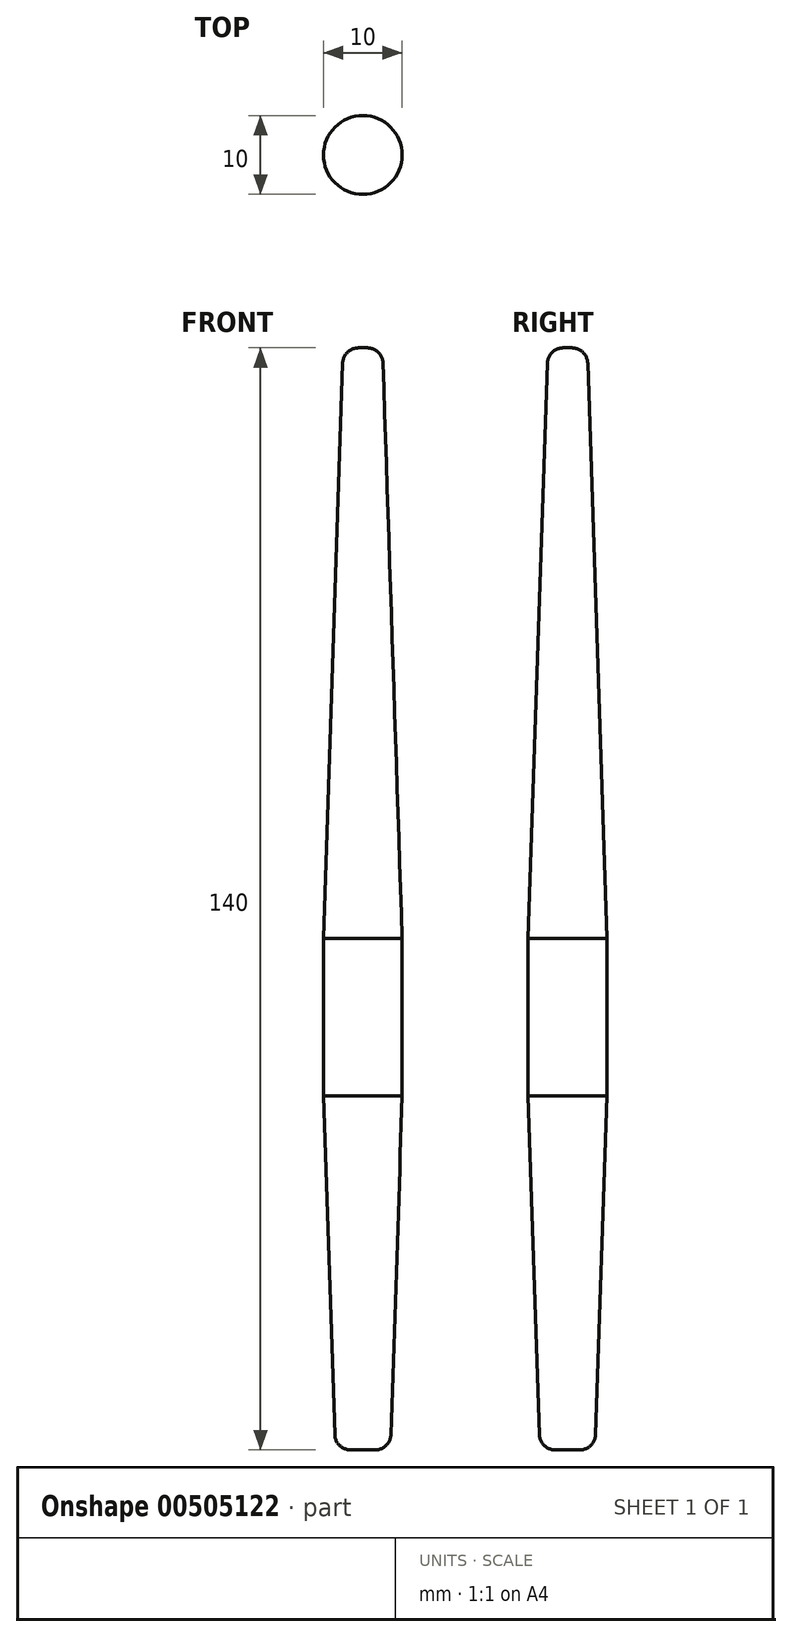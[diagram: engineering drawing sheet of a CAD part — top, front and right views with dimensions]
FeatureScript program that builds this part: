
annotation { "Feature Type Name" : "Feature", "Feature Type Description" : "" }
export const myFeature = defineFeature(function(context is Context, id is Id, definition is map)
    precondition{}
    {
        {
            var Q0;
            Q0=qCreatedBy(makeId("Top.planeOp"),FACE);
            var sketch = newSketch(context, id + "F0", { "sketchPlane" : qUnion([Q0])});
            skCircle(sketch, "E0", {"center": v(0, 0) * mm, "radius": 3.5 * mm});
            skSolve(sketch);
        }
        {
            var Q0;
            Q0=qCreatedBy(makeId("Top.planeOp"),FACE);
            cPlane(context, id + "F1", {"entities" : qUnion([Q0]), "cplaneType" : CPlaneType.OFFSET, "offset" : 45 * mm, "width" : 150 * mm, "height" : 150 * mm});
        }
        {
            var Q0;
            Q0=qCreatedBy(id+"F1.planeOp",FACE);
            var sketch = newSketch(context, id + "F2", { "sketchPlane" : qUnion([Q0])});
            skCircle(sketch, "E1", {"center": v(0, 0) * mm, "radius": 5 * mm});
            skSolve(sketch);
        }
        {
            var Q0;
            Q0=makeQuery(id+"F2.imprint","IMPRINT",FACE,{"disambiguationData":[TD([[makeQuery(id+"F2.imprint","IMPRINT",EDGE,{"derivedFrom":sQuery(id+"F2.wireOp",EDGE,"E1")}),1.0]])]});
            var Q1;
            Q1=makeQuery(id+"F0.imprint","IMPRINT",FACE,{"disambiguationData":[TD([[makeQuery(id+"F0.imprint","IMPRINT",EDGE,{"derivedFrom":sQuery(id+"F0.wireOp",EDGE,"E0")}),1.0]])]});
            loft(context, id + "F3", {"sheetProfilesArray" : [{ "sheetProfileEntities" : qUnion([Q0]) }, { "sheetProfileEntities" : qUnion([Q1]) }]});
        }
        {
            var Q0;
            Q0=makeQuery(id+"F3.opLoft","MID_CAP_EDGE",EDGE,{"disambiguationData":[OSD([sQuery(id+"F0.wireOp",EDGE,"E0"),sQuery(id+"F2.wireOp",EDGE,"E1")])],"capPos":1.0});
            fillet(context, id + "F4", {"entities" : qUnion([Q0]), "radius" : 2 * mm, "tangentPropagation" : true, "allowEdgeOverflow" : false});
        }
        {
            var Q0;
            Q0=qCreatedBy(id+"F1.planeOp",FACE);
            cPlane(context, id + "F5", {"entities" : qUnion([Q0]), "cplaneType" : CPlaneType.OFFSET, "offset" : 20 * mm, "width" : 150 * mm, "height" : 150 * mm});
        }
        {
            var Q0;
            Q0=qCreatedBy(id+"F5.planeOp",FACE);
            var sketch = newSketch(context, id + "F6", { "sketchPlane" : qUnion([Q0])});
            skCircle(sketch, "E2", {"center": v(0, 0) * mm, "radius": 5 * mm});
            skSolve(sketch);
        }
        {
            var Q1;
            Q1=makeQuery(id+"F3.opLoft","CAP_FACE",FACE,{"disambiguationData":[OSD([makeQuery(id+"F2.imprint","IMPRINT",FACE,{"disambiguationData":[TD([[makeQuery(id+"F2.imprint","IMPRINT",EDGE,{"derivedFrom":sQuery(id+"F2.wireOp",EDGE,"E1")}),1.0]])]})])],"isStart":true});
            var Q2;
            Q2=makeQuery(id+"F6.imprint","IMPRINT",FACE,{"disambiguationData":[TD([[makeQuery(id+"F6.imprint","IMPRINT",EDGE,{"derivedFrom":sQuery(id+"F6.wireOp",EDGE,"E2")}),1.0]])]});
            loft(context, id + "F7", {"operationType" : NewBodyOperationType.ADD, "sheetProfilesArray" : [{ "sheetProfileEntities" : qUnion([Q1]) }, { "sheetProfileEntities" : qUnion([Q2]) }]});
        }
        {
            var Q0;
            Q0=qCreatedBy(id+"F5.planeOp",FACE);
            cPlane(context, id + "F8", {"entities" : qUnion([Q0]), "cplaneType" : CPlaneType.OFFSET, "offset" : 75 * mm, "width" : 150 * mm, "height" : 150 * mm});
        }
        {
            var Q0;
            Q0=qCreatedBy(id+"F8.planeOp",FACE);
            var sketch = newSketch(context, id + "F9", { "sketchPlane" : qUnion([Q0])});
            skCircle(sketch, "E3", {"center": v(0, 0) * mm, "radius": 2.5 * mm});
            skSolve(sketch);
        }
        {
            var Q1;
            Q1=makeQuery(id+"F7.opLoft","CAP_FACE",FACE,{"disambiguationData":[OSD([makeQuery(id+"F6.imprint","IMPRINT",FACE,{"disambiguationData":[TD([[makeQuery(id+"F6.imprint","IMPRINT",EDGE,{"derivedFrom":sQuery(id+"F6.wireOp",EDGE,"E2")}),1.0]])]})])],"isStart":true});
            var Q2;
            Q2=makeQuery(id+"F9.imprint","IMPRINT",FACE,{"disambiguationData":[TD([[makeQuery(id+"F9.imprint","IMPRINT",EDGE,{"derivedFrom":sQuery(id+"F9.wireOp",EDGE,"E3")}),1.0]])]});
            loft(context, id + "F10", {"operationType" : NewBodyOperationType.ADD, "sheetProfilesArray" : [{ "sheetProfileEntities" : qUnion([Q1]) }, { "sheetProfileEntities" : qUnion([Q2]) }]});
        }
        {
            var Q0;
            Q0=makeQuery(id+"F10.opLoft","MID_CAP_EDGE",EDGE,{"disambiguationData":[OSD([sQuery(id+"F2.wireOp",EDGE,"E1"),sQuery(id+"F6.wireOp",EDGE,"E2"),sQuery(id+"F9.wireOp",EDGE,"E3")])],"capPos":1.0});
            fillet(context, id + "F11", {"entities" : qUnion([Q0]), "radius" : 2 * mm, "tangentPropagation" : true, "allowEdgeOverflow" : false});
        }
    });
